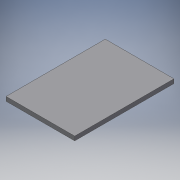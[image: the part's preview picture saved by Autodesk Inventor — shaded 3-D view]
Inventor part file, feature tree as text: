
AUTODESK INVENTOR PART (.ipt)
format: ipt  version: 2018 (Build 220112000, 112)  size: 88,576 bytes
history: native  units: mm
features: other x1, extrude x1, sketch x1
ambient origin geometry x8: Origin, YZ Plane, XZ Plane, XY Plane, X Axis, Y Axis, Z Axis, Center Point
bodies: Body1 (feature_tree)
feature tree (3):
  other  "Sólido1"
  extrude  "Extrusão1"  [1 undecoded]
  sketch  "Esboço1"  dims[d0=6.35mm d1=0.0mm]
note: 1 required parameter value undecoded (feature->parameter linkage not recoverable at this tier; creation-order binding heuristic only, values carry confidence <= 0.55)
